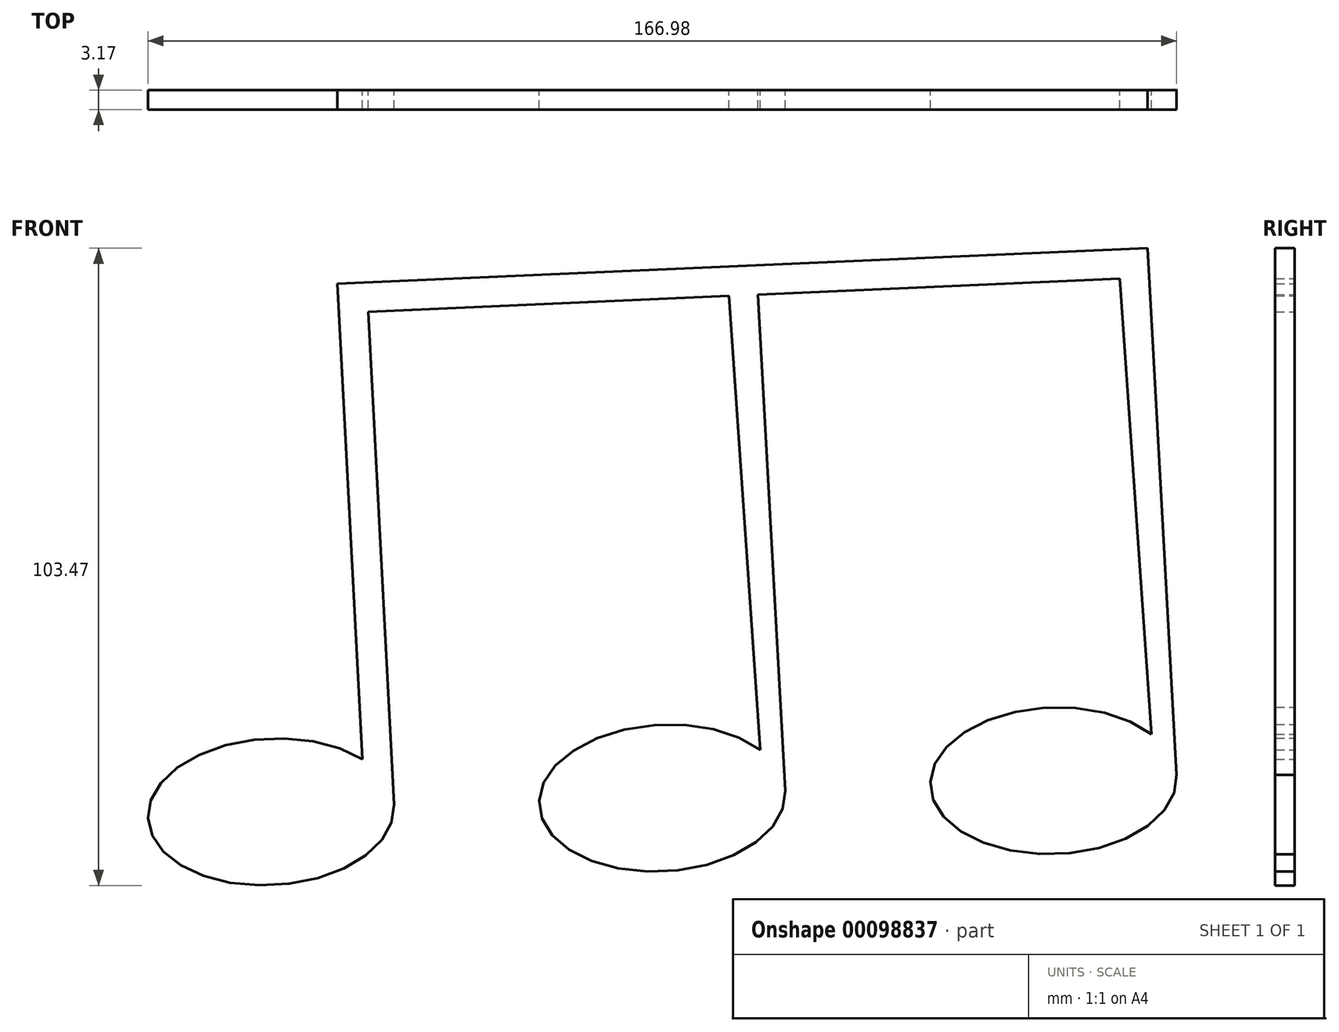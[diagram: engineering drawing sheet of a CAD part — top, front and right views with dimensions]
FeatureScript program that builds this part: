
annotation { "Feature Type Name" : "Feature", "Feature Type Description" : "" }
export const myFeature = defineFeature(function(context is Context, id is Id, definition is map)
    precondition{}
    {
        {
            var Q0;
            Q0=qCreatedBy(makeId("Front.planeOp"),FACE);
            var sketch = newSketch(context, id + "F0", { "sketchPlane" : qUnion([Q0])});
            skEllipticalArc(sketch, "E0", {});
            skLineSegment(sketch, "E1", {"start": v(-57.47, 34.6) * mm, "end": v(-53.45, -42.58) * mm});
            skEllipticalArc(sketch, "E2", {});
            skLineSegment(sketch, "E3", {"start": v(-48.3, -49.98) * mm, "end": v(-52.47, 30.05) * mm});
            skLineSegment(sketch, "E4", {"start": v(-52.47, 30.05) * mm, "end": v(6.03, 32.64) * mm});
            skLineSegment(sketch, "E5", {"start": v(6.03, 32.64) * mm, "end": v(11.12, -41.06) * mm});
            skEllipticalArc(sketch, "E6", {});
            skLineSegment(sketch, "E7", {"start": v(78.72, -45.38) * mm, "end": v(74.03, 40.4) * mm});
            skLineSegment(sketch, "E8", {"start": v(-57.47, 34.6) * mm, "end": v(74.03, 40.4) * mm});
            skLineSegment(sketch, "E9", {"start": v(15.2, -47.73) * mm, "end": v(10.8, 32.83) * mm});
            skLineSegment(sketch, "E10", {"start": v(74.64, -38.5) * mm, "end": v(69.54, 35.44) * mm});
            skLineSegment(sketch, "E11", {"start": v(10.8, 32.83) * mm, "end": v(69.54, 35.44) * mm});
            const initialGuessF0  = {"E0": [-0.06826909290669897, -0.051123909935247666, -0.9983503663845338, -0.05741555485987356, 0.020002500000000003, 0.011906250000000002, 3.8429288138539346, 3.141592653589793], "E2": [-0.004769092906698969, -0.0488816802130686, -0.9983503663845338, -0.057415554859873874, 0.020002500000000003, 0.011906250000000002, 3.75890387354027, 3.141592653589793], "E6": [0.05873090709330103, -0.04607965118914773, 0.9993844003803591, 0.03508304827676903, 0.020002500000000003, 0.011906250000000002, 0.6300081076520745, 0.02320698452475473]};
            skSetInitialGuess(sketch, initialGuessF0);
            skSolve(sketch);
        }
        {
            var Q0;
            Q0 = qSketchRegion(id + "F0", true);
            extrude(context, id + "F1", {"entities" : qUnion([Q0]), "depth" : 3.17 * mm});
        }
    });
